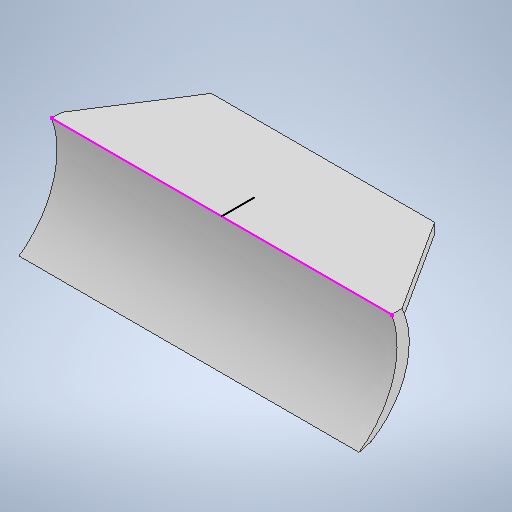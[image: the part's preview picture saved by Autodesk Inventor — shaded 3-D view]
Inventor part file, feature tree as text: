
AUTODESK INVENTOR PART (.ipt)
format: ipt  version: 2025.1 (Build 291241020, 241B)  size: 375,808 bytes
history: native  units: in
note: dims shown in document units (in); Inventor stores cm internally (conversion verified against a paired STEP export)
features: sketch x14, extrude x13
ambient origin geometry x8: Origin, YZ Plane, XZ Plane, XY Plane, X Axis, Y Axis, Z Axis, Center Point
bodies: Solid1 (feature_tree)
feature tree (27):
  extrude  "Extrusion1"  Depth=2.5591in
  extrude  "Extrusion2"  Depth=0.9843in TaperAngle=0.0deg
  extrude  "Extrusion3"  TaperAngle=165.0deg  [1 undecoded]
  extrude  "Extrusion4"  Depth=0.9843in TaperAngle=0.0deg
  sketch  "Sketch5"  dims[d12=0.4134in d13=0.2067in]
  extrude  "Extrusion5"  Depth=0.2067in
  extrude  "Extrusion6"  Depth=0.7382in
  sketch  "Sketch12"  dims[d16=0.7382in d17=0.1201in]
  extrude  "Extrusion12"  Depth=0.1201in
  extrude  "Extrusion13"  Depth=0.1201in
  extrude  "Extrusion14"  Depth=0.1181in
  extrude  "Extrusion15"  Depth=0.1181in
  extrude  "Extrusion16"  Depth=0.0984in TaperAngle=0.0deg
  sketch  "Sketch20"  dims[d60=0.3714in d62=0.139in]
  extrude  "Extrusion18"  Depth=0.7874in
  extrude  "Extrusion19"  Depth=0.139in
  sketch  "Sketch1"  dims[d0=1.2795in d1=2.5591in]
  sketch  "Sketch2"  dims[d2=0.748in d3=0.9843in d4=0.0in]
  sketch  "Sketch3"  dims[d5=0.4331in d6=165.0deg]
  sketch  "Sketch4"  dims[d7=0.9843in d8=0.0in d10=3.2062in d11=0.0in]
  sketch  "Sketch6"  dims[d14=0.5413in d15=0.7382in]
  sketch  "Sketch14"  dims[d18=0.1201in d19=0.1201in]
  sketch  "Sketch15"  dims[d20=0.1575in d21=0.0in d22=0.1181in]
  sketch  "Sketch16"  dims[d23=0.3937in d24=0.1181in]
  sketch  "Sketch17"  dims[d25=0.0984in d26=4.47in d27=0.0in]
  sketch  "Sketch18"  dims[d28=0.7874in d29=0.0in d59=1.1811in]
  sketch  "Sketch21"  dims[d63=15.0deg d64=0.3937in d65=0.0in d66=0.1181in d67=2.5591in d68=0.0in d69=0.1181in d70=0.6693in d71=0.0in d72=0.1181in d73=0.6693in d74=0.0in d75=2.6068in d76=0.0in d81=4.8937in d82=0.0in d83=4.8937in d84=0.0in d46=0.0197in d47=0.0344in d48=0.0197in d49=0.0344in d85=0.0197in d86=0.0344in]
note: 1 required parameter value undecoded (feature->parameter linkage not recoverable at this tier; creation-order binding heuristic only, values carry confidence <= 0.55)
